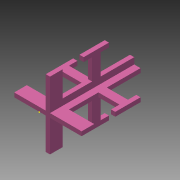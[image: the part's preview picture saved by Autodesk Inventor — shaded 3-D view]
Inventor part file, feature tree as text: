
AUTODESK INVENTOR PART (.ipt)
format: ipt  version: 2015 (Build 190159000, 159)  size: 192,000 bytes
history: native  units: mm
features: sketch x11, extrude x10
ambient origin geometry x8: Origin, YZ Plane, XZ Plane, XY Plane, X Axis, Y Axis, Z Axis, Center Point
bodies: Solide1 (feature_tree)
feature tree (21):
  sketch  "Esquisse1"
  extrude  "Extrusion1"  Depth=100.0mm
  extrude  "Extrusion2"  Depth=20.0mm
  extrude  "Extrusion3"  Depth=5.0mm TaperAngle=0.0deg
  extrude  "Extrusion4"  Depth=7.5mm
  extrude  "Extrusion5"  Depth=7.5mm
  extrude  "Extrusion6"  Depth=7.5mm TaperAngle=0.0deg
  extrude  "Extrusion7"  Depth=15.0mm
  extrude  "Extrusion8"  Depth=30.0mm TaperAngle=0.0deg
  extrude  "Extrusion9"  Depth=15.0mm
  extrude  "Extrusion10"  Depth=30.0mm TaperAngle=0.0deg
  sketch  "Esquisse2"
  sketch  "Esquisse3"
  sketch  "Esquisse4"
  sketch  "Esquisse5"
  sketch  "Esquisse6"
  sketch  "Esquisse7"
  sketch  "Esquisse8"
  sketch  "Esquisse9"
  sketch  "Esquisse10"
  sketch  "Esquisse11"
